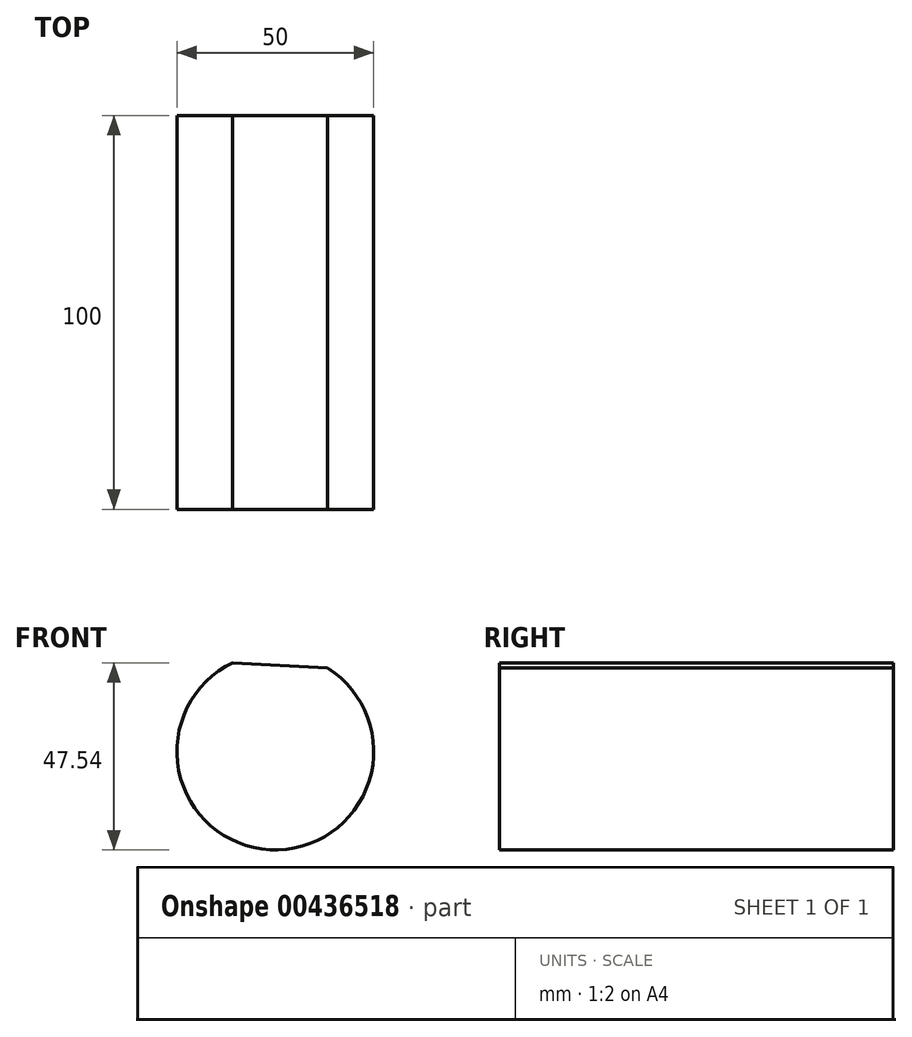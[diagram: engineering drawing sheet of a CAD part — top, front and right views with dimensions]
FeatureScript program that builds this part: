
annotation { "Feature Type Name" : "Feature", "Feature Type Description" : "" }
export const myFeature = defineFeature(function(context is Context, id is Id, definition is map)
    precondition{}
    {
        {
            var Q0;
            Q0=qCreatedBy(makeId("Front.planeOp"),FACE);
            var sketch = newSketch(context, id + "F0", { "sketchPlane" : qUnion([Q0])});
            skCircle(sketch, "E0", {"center": v(0, 0) * mm, "radius": 25 * mm});
            skLineSegment(sketch, "E1", {"start": v(0, 0) * mm, "end": v(13.26, 21.2) * mm});
            skLineSegment(sketch, "E2", {"start": v(13.26, 21.2) * mm, "end": v(-10.82, 22.54) * mm});
            skLineSegment(sketch, "E3", {"start": v(-10.82, 22.54) * mm, "end": v(0, 0) * mm});
            skSolve(sketch);
        }
        {
            var Q0;
            Q0 = qSketchRegion(id + "F0", true);
            extrude(context, id + "F1", {"entities" : qUnion([Q0]), "depth" : 100 * mm});
        }
        {
            var Q0;
            {var subQ0=sQuery(id+"F0.wireOp",EDGE,"E2");Q0=makeQuery(id+"F0.imprint","IMPRINT",FACE,{"disambiguationData":[TD([[makeQuery(id+"F0.imprint","IMPRINT",EDGE,{"derivedFrom":subQ0}),-1.0]])]});}
            extrude(context, id + "F2", {"entities" : qUnion([Q0]), "operationType" : NewBodyOperationType.REMOVE, "depth" : (100) * mm});
        }
    });
